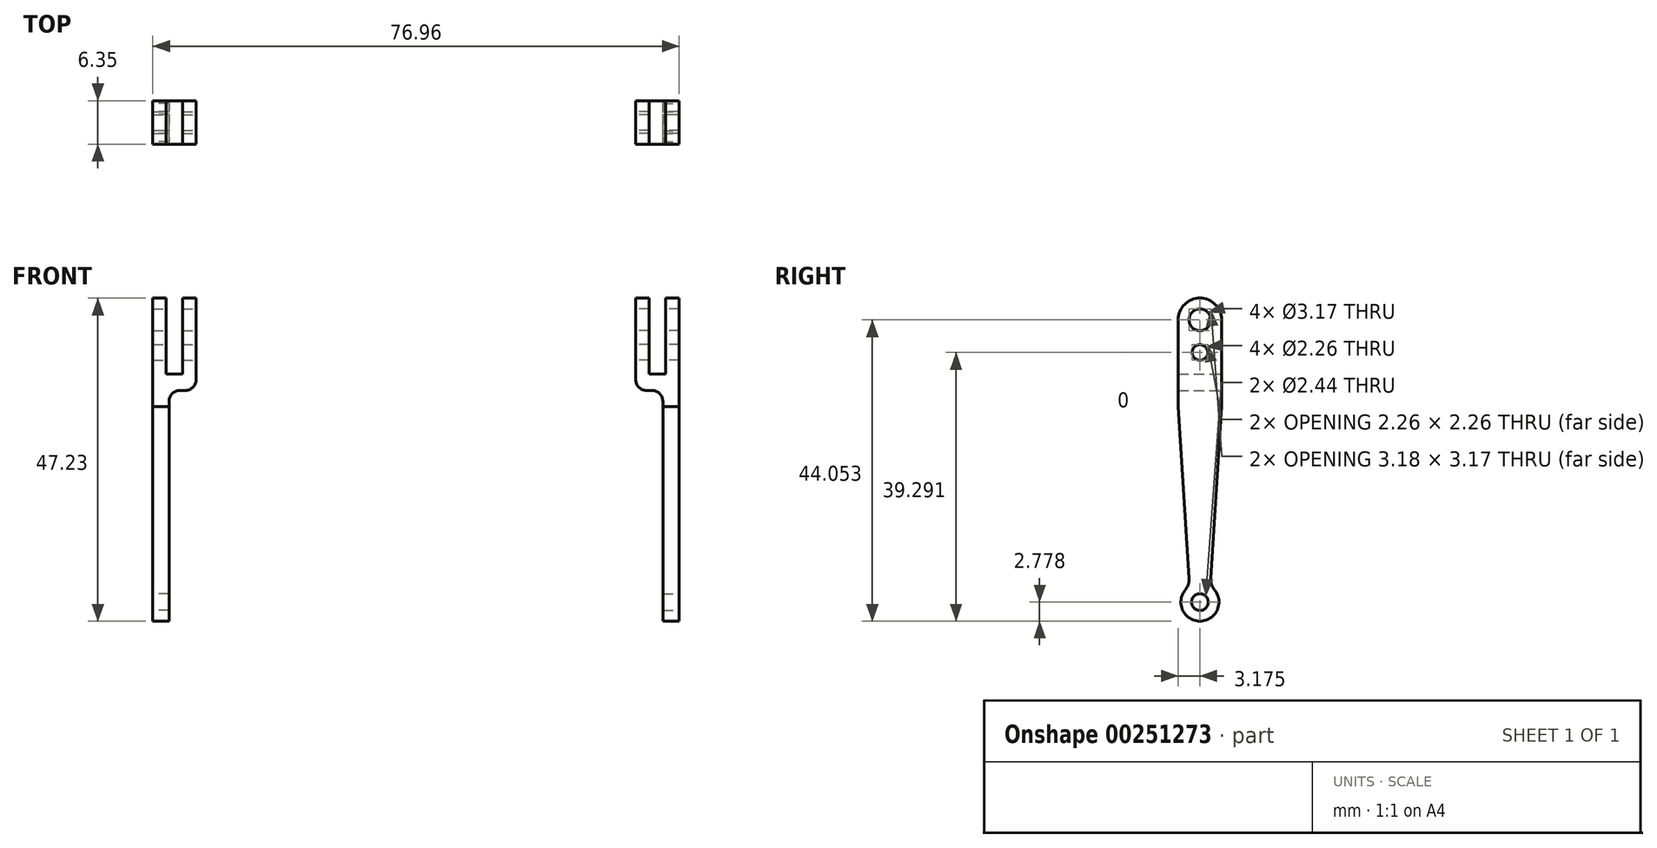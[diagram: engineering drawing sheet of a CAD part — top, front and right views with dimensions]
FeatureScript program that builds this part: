
annotation { "Feature Type Name" : "Feature", "Feature Type Description" : "" }
export const myFeature = defineFeature(function(context is Context, id is Id, definition is map)
    precondition{}
    {
        {
            var Q0;
            Q0=qCreatedBy(makeId("Front.planeOp"),FACE);
            var sketch = newSketch(context, id + "F0", { "sketchPlane" : qUnion([Q0])});
            skLineSegment(sketch, "E0", {"start": v(38.48, 4.76) * mm, "end": v(38.48, 51.99) * mm});
            skLineSegment(sketch, "E1", {"start": v(38.48, 51.99) * mm, "end": v(36.5, 51.99) * mm});
            skLineSegment(sketch, "E2", {"start": v(36.5, 51.99) * mm, "end": v(36.5, 40.88) * mm});
            skLineSegment(sketch, "E3", {"start": v(36.5, 40.88) * mm, "end": v(34.12, 40.88) * mm});
            skLineSegment(sketch, "E4", {"start": v(34.12, 40.88) * mm, "end": v(34.12, 51.99) * mm});
            skLineSegment(sketch, "E5", {"start": v(34.12, 51.99) * mm, "end": v(32.13, 51.99) * mm});
            skLineSegment(sketch, "E6", {"start": v(32.13, 51.99) * mm, "end": v(32.13, 38.5) * mm});
            skLineSegment(sketch, "E7", {"start": v(32.13, 38.5) * mm, "end": v(36.1, 38.5) * mm});
            skLineSegment(sketch, "E8", {"start": v(36.1, 38.5) * mm, "end": v(36.1, 4.76) * mm});
            skLineSegment(sketch, "E9", {"start": v(36.1, 4.76) * mm, "end": v(38.48, 4.76) * mm});
            skSolve(sketch);
        }
        {
            var Q0;
            Q0 = qSketchRegion(id + "F0", true);
            extrude(context, id + "F1", {"entities" : qUnion([Q0]), "depth" : 6.35 * mm});
        }
        {
            var Q0;
            Q0=makeQuery(id+"F1.opExtrude","SWEPT_EDGE",EDGE,{"disambiguationData":[OSD([sQuery(id+"F0.wireOp",EDGE,"E7"),sQuery(id+"F0.wireOp",EDGE,"E8")])]});
            var Q1;
            Q1=makeQuery(id+"F1.opExtrude","SWEPT_EDGE",EDGE,{"disambiguationData":[OSD([sQuery(id+"F0.wireOp",EDGE,"E6"),sQuery(id+"F0.wireOp",EDGE,"E7")])]});
            fillet(context, id + "F2", {"entities" : qUnion([Q0, Q1]), "radius" : 1.59 * mm, "tangentPropagation" : true, "allowEdgeOverflow" : false});
        }
        {
            var Q0;
            Q0=makeQuery(id+"F1.opExtrude","CAP_EDGE",EDGE,{"disambiguationData":[OSD([sQuery(id+"F0.wireOp",EDGE,"E5")])],"isStart":false});
            var Q1;
            Q1=makeQuery(id+"F1.opExtrude","CAP_EDGE",EDGE,{"disambiguationData":[OSD([sQuery(id+"F0.wireOp",EDGE,"E5")])],"isStart":true});
            var Q2;
            Q2=makeQuery(id+"F1.opExtrude","CAP_EDGE",EDGE,{"disambiguationData":[OSD([sQuery(id+"F0.wireOp",EDGE,"E1")])],"isStart":true});
            var Q3;
            Q3=makeQuery(id+"F1.opExtrude","CAP_EDGE",EDGE,{"disambiguationData":[OSD([sQuery(id+"F0.wireOp",EDGE,"E1")])],"isStart":false});
            fillet(context, id + "F3", {"entities" : qUnion([Q0, Q1, Q2, Q3]), "radius" : 3.17 * mm, "tangentPropagation" : true, "allowEdgeOverflow" : false});
        }
        {
            var Q0;
            Q0=makeQuery(id+"F1.opExtrude","SWEPT_FACE",FACE,{"disambiguationData":[OSD([sQuery(id+"F0.wireOp",EDGE,"E0")])]});
            var sketch = newSketch(context, id + "F4", { "sketchPlane" : qUnion([Q0])});
            skPoint(sketch, "E10", {"position": v(-3.18, 48.81) * mm});
            skPoint(sketch, "E11", {"position": v(-3.18, 44.05) * mm});
            skSolve(sketch);
        }
        {
            var Q0;
            Q0=sQuery(id+"F4.wireOp",VERTEX,"E10");
            var Q1;
            Q1=makeQuery(id+"F1.opExtrude","SWEPT_BODY",BODY,{"disambiguationData":[OSD([sQuery(id+"F0.wireOp",EDGE,"E0"),sQuery(id+"F0.wireOp",EDGE,"E1"),sQuery(id+"F0.wireOp",EDGE,"E2"),sQuery(id+"F0.wireOp",EDGE,"E3"),sQuery(id+"F0.wireOp",EDGE,"E4"),sQuery(id+"F0.wireOp",EDGE,"E5"),sQuery(id+"F0.wireOp",EDGE,"E6"),sQuery(id+"F0.wireOp",EDGE,"E7"),sQuery(id+"F0.wireOp",EDGE,"E8"),sQuery(id+"F0.wireOp",EDGE,"E9")])]});
            hole(context, id + "F5", {"style" : HoleStyle.SIMPLE, "endStyle" : HoleEndStyle.THROUGH, "holeDiameter" : 3.17 * mm, "tappedDepth" : 12.7 * mm, "tapClearance" : 3, "locations" : qUnion([Q0]), "scope" : qUnion([Q1]), "startStyle" : HoleStartStyle.PART});
        }
        {
            var Q0;
            Q0=makeQuery(id+"F1.opExtrude","SWEPT_FACE",FACE,{"disambiguationData":[OSD([sQuery(id+"F0.wireOp",EDGE,"E0")])]});
            var sketch = newSketch(context, id + "F6", { "sketchPlane" : qUnion([Q0])});
            skPoint(sketch, "E12", {"position": v(-3.18, 44.05) * mm});
            skSolve(sketch);
        }
        {
            var Q0;
            Q0=sQuery(id+"F6.wireOp",VERTEX,"E12");
            var Q1;
            Q1=makeQuery(id+"F1.opExtrude","SWEPT_BODY",BODY,{"disambiguationData":[OSD([sQuery(id+"F0.wireOp",EDGE,"E0"),sQuery(id+"F0.wireOp",EDGE,"E1"),sQuery(id+"F0.wireOp",EDGE,"E2"),sQuery(id+"F0.wireOp",EDGE,"E3"),sQuery(id+"F0.wireOp",EDGE,"E4"),sQuery(id+"F0.wireOp",EDGE,"E5"),sQuery(id+"F0.wireOp",EDGE,"E6"),sQuery(id+"F0.wireOp",EDGE,"E7"),sQuery(id+"F0.wireOp",EDGE,"E8"),sQuery(id+"F0.wireOp",EDGE,"E9")])]});
            hole(context, id + "F7", {"style" : HoleStyle.SIMPLE, "endStyle" : HoleEndStyle.THROUGH, "holeDiameter" : 2.26 * mm, "tappedDepth" : 12.7 * mm, "tapClearance" : 3, "locations" : qUnion([Q0]), "scope" : qUnion([Q1]), "startStyle" : HoleStartStyle.PART});
        }
        {
            var Q0;
            Q0=makeQuery(id+"F1.opExtrude","SWEPT_FACE",FACE,{"disambiguationData":[OSD([sQuery(id+"F0.wireOp",EDGE,"E0")])]});
            var sketch = newSketch(context, id + "F8", { "sketchPlane" : qUnion([Q0])});
            skCircle(sketch, "E13", {"center": v(-3.18, 7.54) * mm, "radius": 1.22 * mm});
            skCircle(sketch, "E14", {"center": v(-3.18, 7.54) * mm, "radius": 2.78 * mm});
            skLineSegment(sketch, "E15", {"start": v(-6.35, 36.11) * mm, "end": v(0, 36.11) * mm});
            skLineSegment(sketch, "E16", {"start": v(-6.35, 11.06) * mm, "end": v(0, 11.06) * mm});
            skLineSegment(sketch, "E17", {"start": v(-6.35, 36.11) * mm, "end": v(-4.76, 11.06) * mm});
            skLineSegment(sketch, "E18", {"start": v(0, 36.11) * mm, "end": v(-1.59, 11.06) * mm});
            skArc(sketch, "E19", {"start": v(-5.33, 9.3) * mm, "mid": v(-4.88, 10.12) * mm, "end": v(-4.76, 11.06) * mm});
            skArc(sketch, "E20", {"start": v(-1.59, 11.06) * mm, "mid": v(-1.47, 10.12) * mm, "end": v(-1.02, 9.3) * mm});
            skSolve(sketch);
        }
        {
            var Q0;
            {var subQ3=sQuery(id+"F8.wireOp",EDGE,"E17");Q0=makeQuery(id+"F8.imprint","IMPRINT",FACE,{"disambiguationData":[TD([[makeQuery(id+"F8.imprint","IMPRINT",EDGE,{"derivedFrom":subQ3}),-1.0]])]});}
            var Q1;
            {var subQ8=sQuery(id+"F8.wireOp",EDGE,"E19");Q1=makeQuery(id+"F8.imprint","IMPRINT",FACE,{"disambiguationData":[TD([[makeQuery(id+"F8.imprint","IMPRINT",EDGE,{"derivedFrom":subQ8}),1.0]])]});}
            var Q2;
            Q2=makeQuery(id+"F8.imprint","IMPRINT",FACE,{"disambiguationData":[TD([[makeQuery(id+"F8.imprint","IMPRINT",EDGE,{"derivedFrom":sQuery(id+"F8.wireOp",EDGE,"E13")}),1.0]])]});
            var Q3;
            {var subQ8=sQuery(id+"F8.wireOp",EDGE,"E20");Q3=makeQuery(id+"F8.imprint","IMPRINT",FACE,{"disambiguationData":[TD([[makeQuery(id+"F8.imprint","IMPRINT",EDGE,{"derivedFrom":subQ8}),1.0]])]});}
            var Q4;
            {var subQ3=sQuery(id+"F8.wireOp",EDGE,"E18");Q4=makeQuery(id+"F8.imprint","IMPRINT",FACE,{"disambiguationData":[TD([[makeQuery(id+"F8.imprint","IMPRINT",EDGE,{"derivedFrom":subQ3}),1.0]])]});}
            extrude(context, id + "F9", {"entities" : qUnion([Q0, Q1, Q2, Q3, Q4]), "operationType" : NewBodyOperationType.REMOVE, "oppositeDirection" : true, "depth" : 25.4 * mm});
        }
        {
            var Q0;
            Q0=qCreatedBy(makeId("Right.planeOp"),FACE);
            var sketch = newSketch(context, id + "F10", { "sketchPlane" : qUnion([Q0])});
            skLineSegment(sketch, "E21.bottom", {"start": v(0, 46.47) * mm, "end": v(29.77, 46.47) * mm});
            skLineSegment(sketch, "E21.top", {"start": v(0, 19.75) * mm, "end": v(29.77, 19.75) * mm});
            skLineSegment(sketch, "E21.left", {"start": v(0, 46.47) * mm, "end": v(0, 19.75) * mm});
            skLineSegment(sketch, "E21.right", {"start": v(29.77, 46.47) * mm, "end": v(29.77, 19.75) * mm});
            skSolve(sketch);
        }
        {
            var Q0;
            Q0=makeQuery(id+"F1.opExtrude","SWEPT_BODY",BODY,{"disambiguationData":[OSD([sQuery(id+"F0.wireOp",EDGE,"E0"),sQuery(id+"F0.wireOp",EDGE,"E1"),sQuery(id+"F0.wireOp",EDGE,"E2"),sQuery(id+"F0.wireOp",EDGE,"E3"),sQuery(id+"F0.wireOp",EDGE,"E4"),sQuery(id+"F0.wireOp",EDGE,"E5"),sQuery(id+"F0.wireOp",EDGE,"E6"),sQuery(id+"F0.wireOp",EDGE,"E7"),sQuery(id+"F0.wireOp",EDGE,"E8"),sQuery(id+"F0.wireOp",EDGE,"E9")])]});
            var Q1;
            Q1=makeQuery(id+"F10.imprint","IMPRINT",FACE,{"disambiguationData":[TD([[makeQuery(id+"F10.imprint","IMPRINT",EDGE,{"derivedFrom":sQuery(id+"F10.wireOp",EDGE,"E21.bottom")}),-1.0]])]});
            mirror(context, id + "F11", {"entities" : qUnion([Q0]), "mirrorPlane" : qUnion([Q1])});
        }
    });
